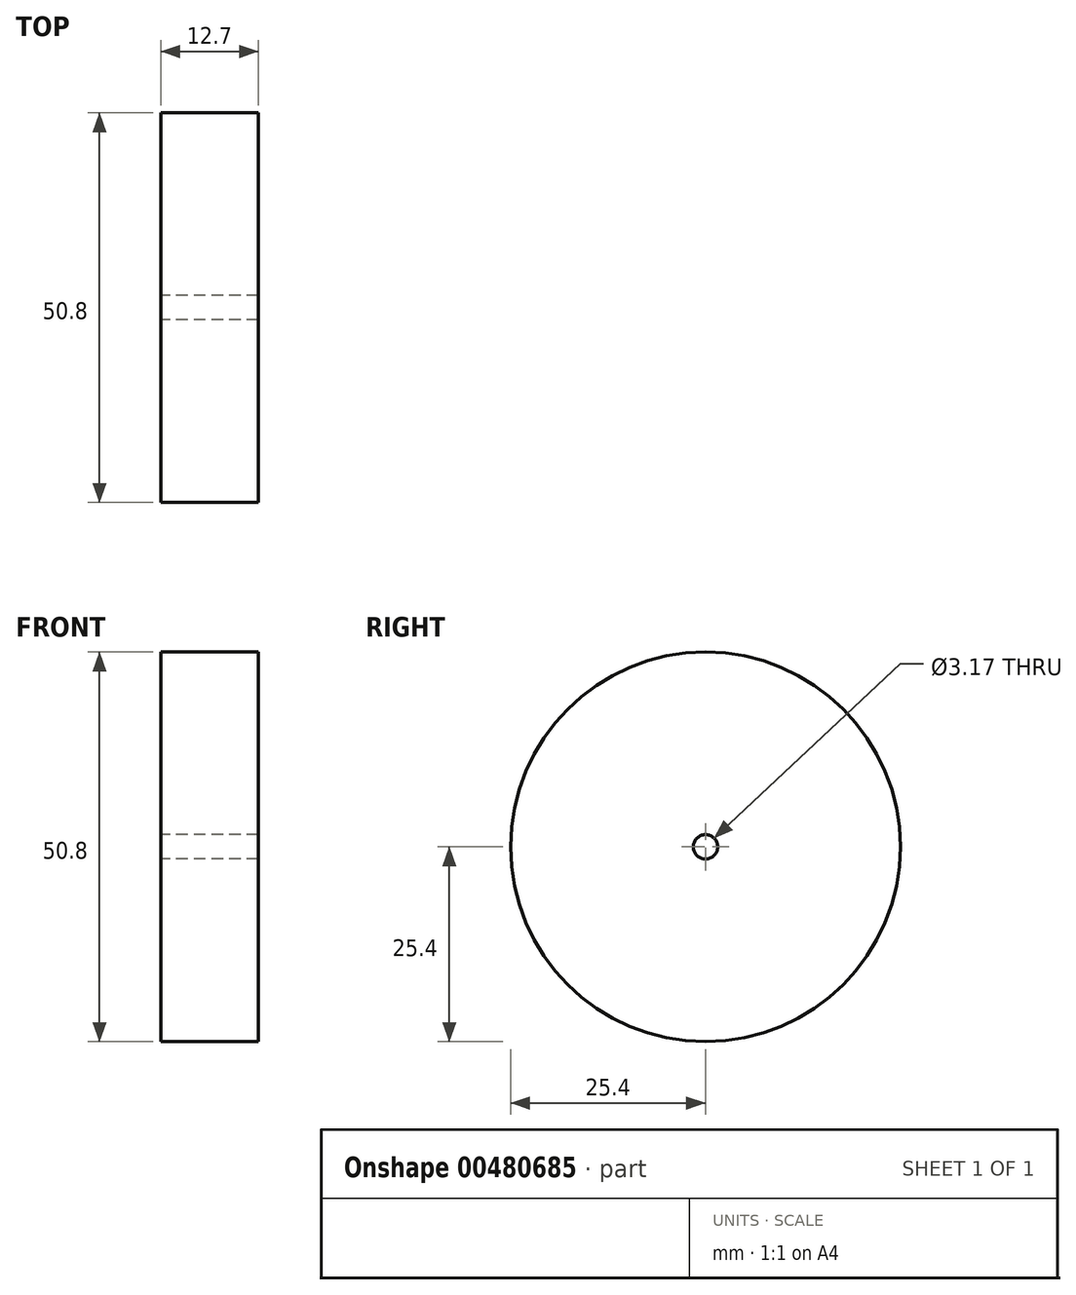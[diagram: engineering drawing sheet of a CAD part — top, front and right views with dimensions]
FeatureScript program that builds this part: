
annotation { "Feature Type Name" : "Feature", "Feature Type Description" : "" }
export const myFeature = defineFeature(function(context is Context, id is Id, definition is map)
    precondition{}
    {
        {
            var Q0;
            Q0=qCreatedBy(makeId("Right.planeOp"),FACE);
            var sketch = newSketch(context, id + "F0", { "sketchPlane" : qUnion([Q0])});
            skCircle(sketch, "E0", {"center": v(0, 0) * mm, "radius": 25.4 * mm});
            skCircle(sketch, "E1", {"center": v(0, 0) * mm, "radius": 1.59 * mm});
            skSolve(sketch);
        }
        {
            var Q0;
            Q0=makeQuery(id+"F0.imprint","IMPRINT",FACE,{"disambiguationData":[TD([[makeQuery(id+"F0.imprint","IMPRINT",EDGE,{"derivedFrom":sQuery(id+"F0.wireOp",EDGE,"E0")}),1.0]])]});
            extrude(context, id + "F1", {"entities" : qUnion([Q0]), "depth" : 12.7 * mm});
        }
    });
